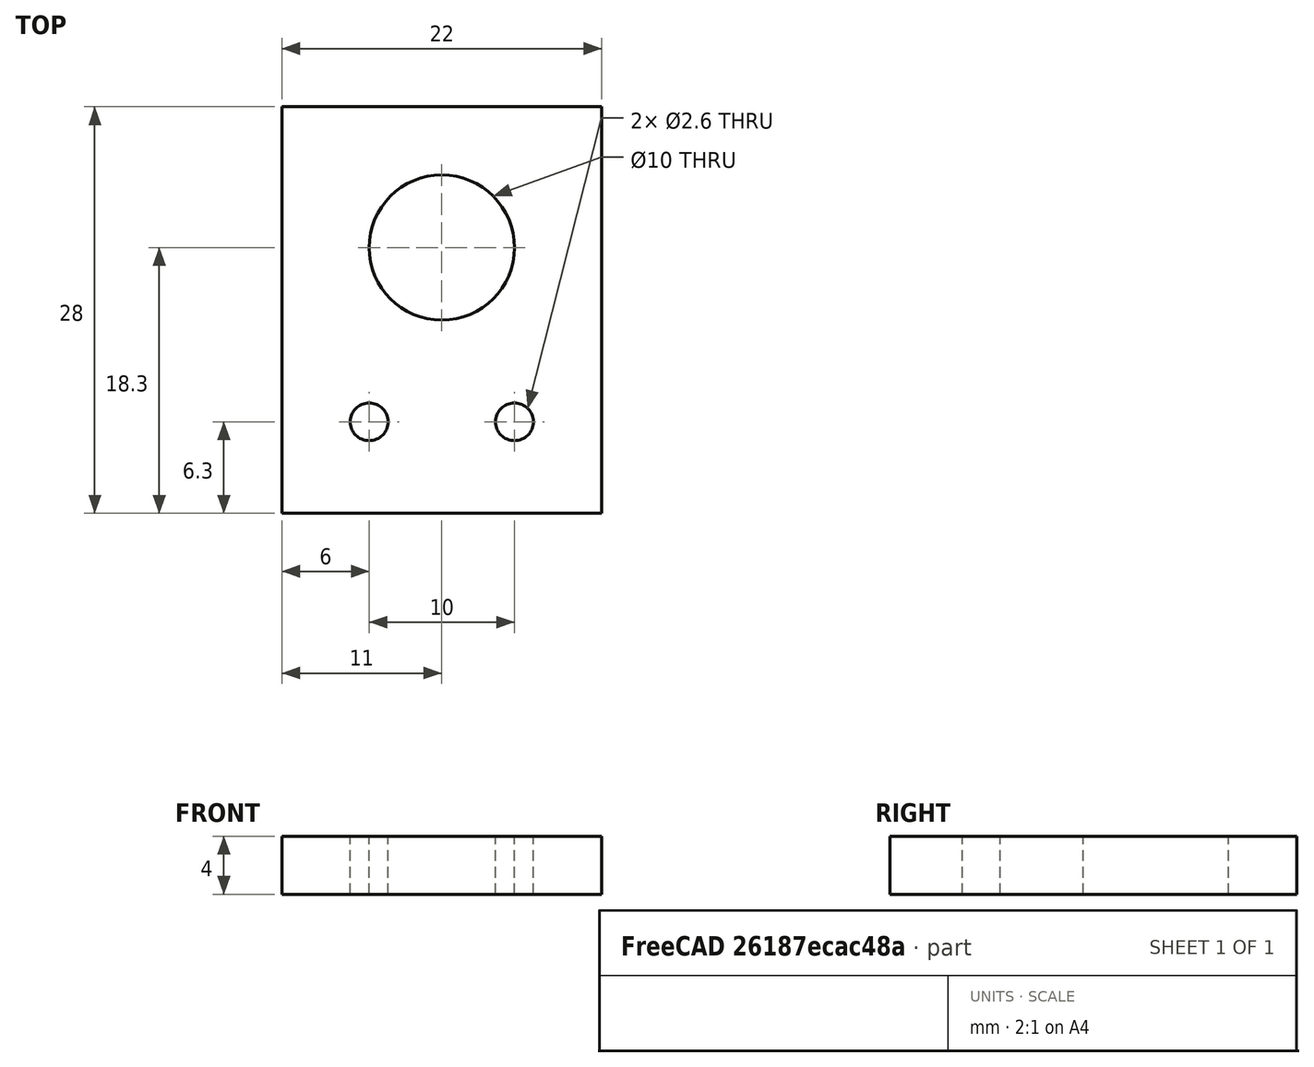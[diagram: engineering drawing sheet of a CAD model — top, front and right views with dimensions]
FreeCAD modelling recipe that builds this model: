
FCSTD DOCUMENT  (FreeCAD 0.18R16110 (Git))
Label: energy-chain-end1
License: All rights reserved
LicenseURL: http://en.wikipedia.org/wiki/All_rights_reserved
objects: Part::Cylinder×3, Part::Cut×3, Mesh::Feature×3, Part::Box×1
note: 7 computed .brp shape members not serialized (recipe doc carries the construction recipe); baked Part::Feature solids carry a one-line shape summary decoded from their .brp

FEATURE [Part::Cylinder] Cylinder099  label="Zylinder087"
  Angle = 360
  AttacherType = Attacher::AttachEngine3D
  Height = 6
  Placement = pos=(42,-23,10) rot=(0,0,1;0rad)
  Radius = 1.3
FEATURE [Part::Box] Box066  label="Quader045"
  AttacherType = Attacher::AttachEngine3D
  Height = 4
  Length = 22
  Placement = pos=(26,-29.3,11) rot=(0,0,1;0rad)
  Width = 28
FEATURE [Part::Cylinder] Cylinder096  label="Zylinder084"
  Angle = 360
  AttacherType = Attacher::AttachEngine3D
  Height = 6
  Placement = pos=(32,-23,10) rot=(0,0,1;0rad)
  Radius = 1.3
FEATURE [Part::Cylinder] Cylinder093  label="Zylinder081"
  Angle = 360
  AttacherType = Attacher::AttachEngine3D
  Height = 10
  Placement = pos=(37,-11,8) rot=(0,0,1;0rad)
  Radius = 5
FEATURE [Part::Cut] Cut106
  Base = -> Box066
  Tool = -> Cylinder099
FEATURE [Part::Cut] Cut107
  Base = -> Cut106
  Tool = -> Cylinder096
FEATURE [Part::Cut] Cut124  label="end-mount"
  Base = -> Cut107
  Tool = -> Cylinder093
FEATURE [Mesh::Feature] Union  label="energy-chain-part"
FEATURE [Mesh::Feature] Mesh  label="end-mount (Meshed)"
FEATURE [Mesh::Feature] Mesh001  label="energy-chain-end1"
